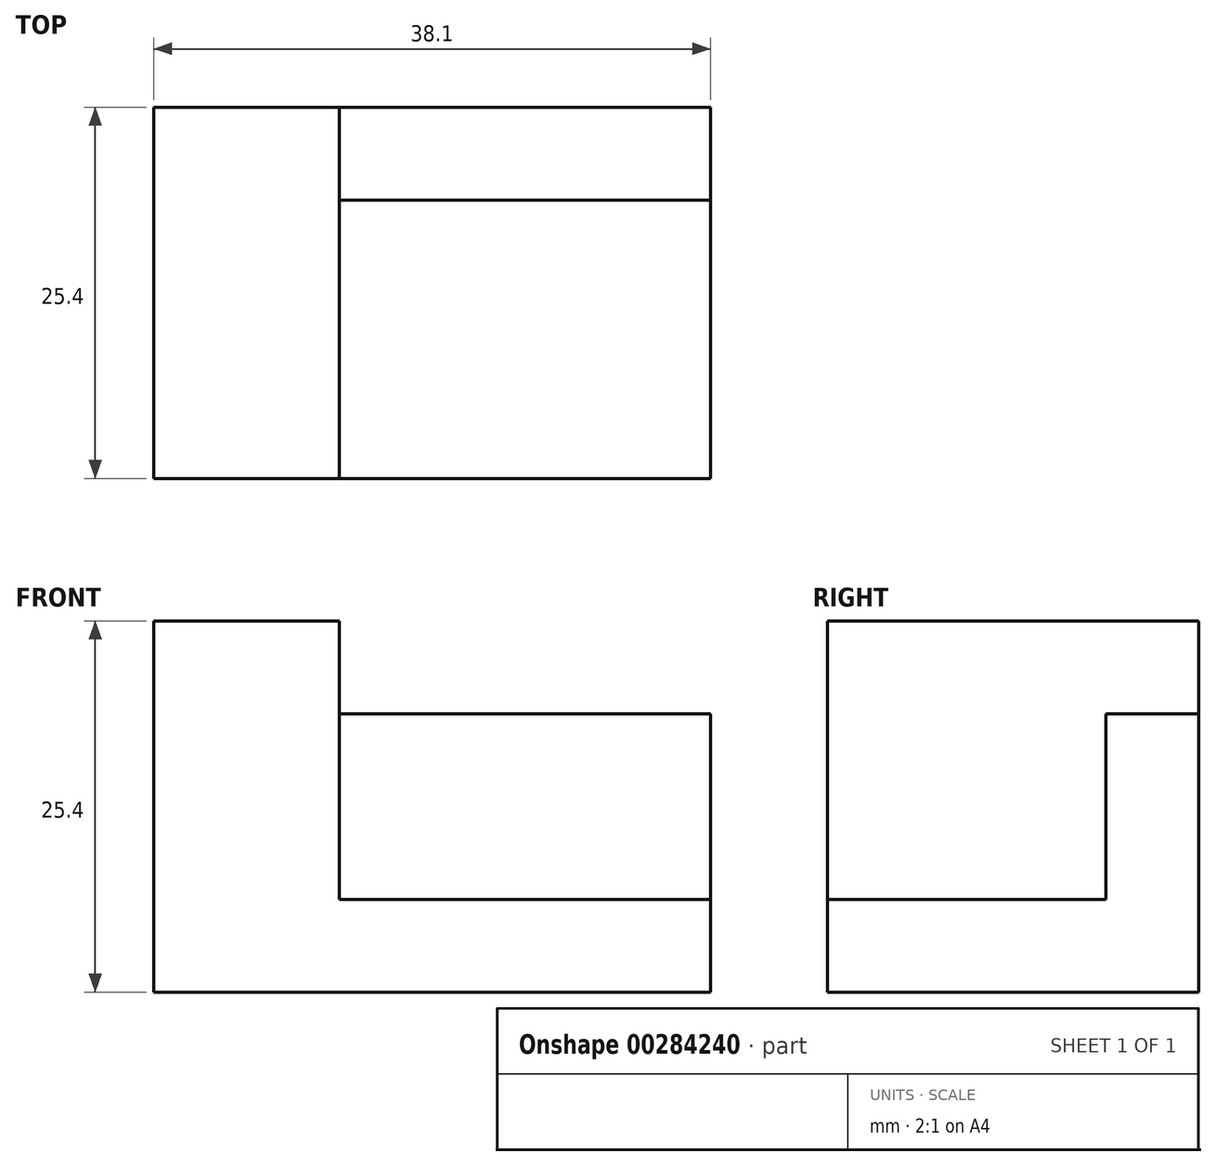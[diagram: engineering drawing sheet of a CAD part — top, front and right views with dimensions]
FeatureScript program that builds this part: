
annotation { "Feature Type Name" : "Feature", "Feature Type Description" : "" }
export const myFeature = defineFeature(function(context is Context, id is Id, definition is map)
    precondition{}
    {
        {
            var Q0;
            Q0=qCreatedBy(makeId("Front.planeOp"),FACE);
            var sketch = newSketch(context, id + "F0", { "sketchPlane" : qUnion([Q0])});
            skLineSegment(sketch, "E0", {"start": v(0, 0) * mm, "end": v(38.1, 0) * mm});
            skLineSegment(sketch, "E1", {"start": v(38.1, 0) * mm, "end": v(38.1, 19.05) * mm});
            skLineSegment(sketch, "E2", {"start": v(38.1, 19.05) * mm, "end": v(12.7, 19.05) * mm});
            skLineSegment(sketch, "E3", {"start": v(12.7, 19.05) * mm, "end": v(12.7, 25.4) * mm});
            skLineSegment(sketch, "E4", {"start": v(12.7, 25.4) * mm, "end": v(0, 25.4) * mm});
            skLineSegment(sketch, "E5", {"start": v(0, 25.4) * mm, "end": v(0, 0) * mm});
            skLineSegment(sketch, "E6", {"start": v(12.7, 19.05) * mm, "end": v(12.7, 6.35) * mm});
            skLineSegment(sketch, "E7", {"start": v(12.7, 6.35) * mm, "end": v(38.1, 6.35) * mm});
            skSolve(sketch);
        }
        {
            var Q0;
            Q0 = qSketchRegion(id + "F0", true);
            extrude(context, id + "F1", {"entities" : qUnion([Q0]), "endBound" : BoundingType.SYMMETRIC, "depth" : 25.4 * mm});
        }
        {
            var Q0;
            Q0=makeQuery(id+"F1.opExtrude","SWEPT_FACE",FACE,{"disambiguationData":[OSD([sQuery(id+"F0.wireOp",EDGE,"E1")])]});
            var sketch = newSketch(context, id + "F2", { "sketchPlane" : qUnion([Q0])});
            skLineSegment(sketch, "E8", {"start": v(-12.7, 0) * mm, "end": v(-12.7, 6.35) * mm});
            skLineSegment(sketch, "E9", {"start": v(-12.7, 6.35) * mm, "end": v(6.35, 6.35) * mm});
            skLineSegment(sketch, "E10", {"start": v(6.35, 6.35) * mm, "end": v(6.35, 19.05) * mm});
            skLineSegment(sketch, "E11", {"start": v(6.35, 19.05) * mm, "end": v(12.7, 19.05) * mm});
            skLineSegment(sketch, "E12", {"start": v(12.7, 19.05) * mm, "end": v(12.7, 0) * mm});
            skLineSegment(sketch, "E13", {"start": v(12.7, 0) * mm, "end": v(-12.7, 0) * mm});
            skSolve(sketch);
        }
        {
            var Q0;
            {var subQ0=sQuery(id+"F2.wireOp",EDGE,"E9");Q0=makeQuery(id+"F2.imprint","IMPRINT",FACE,{"disambiguationData":[TD([[makeQuery(id+"F2.imprint","IMPRINT",EDGE,{"derivedFrom":subQ0}),1.0]])]});}
            extrude(context, id + "F3", {"entities" : qUnion([Q0]), "operationType" : NewBodyOperationType.REMOVE, "oppositeDirection" : true, "depth" : 25.4 * mm});
        }
    });
